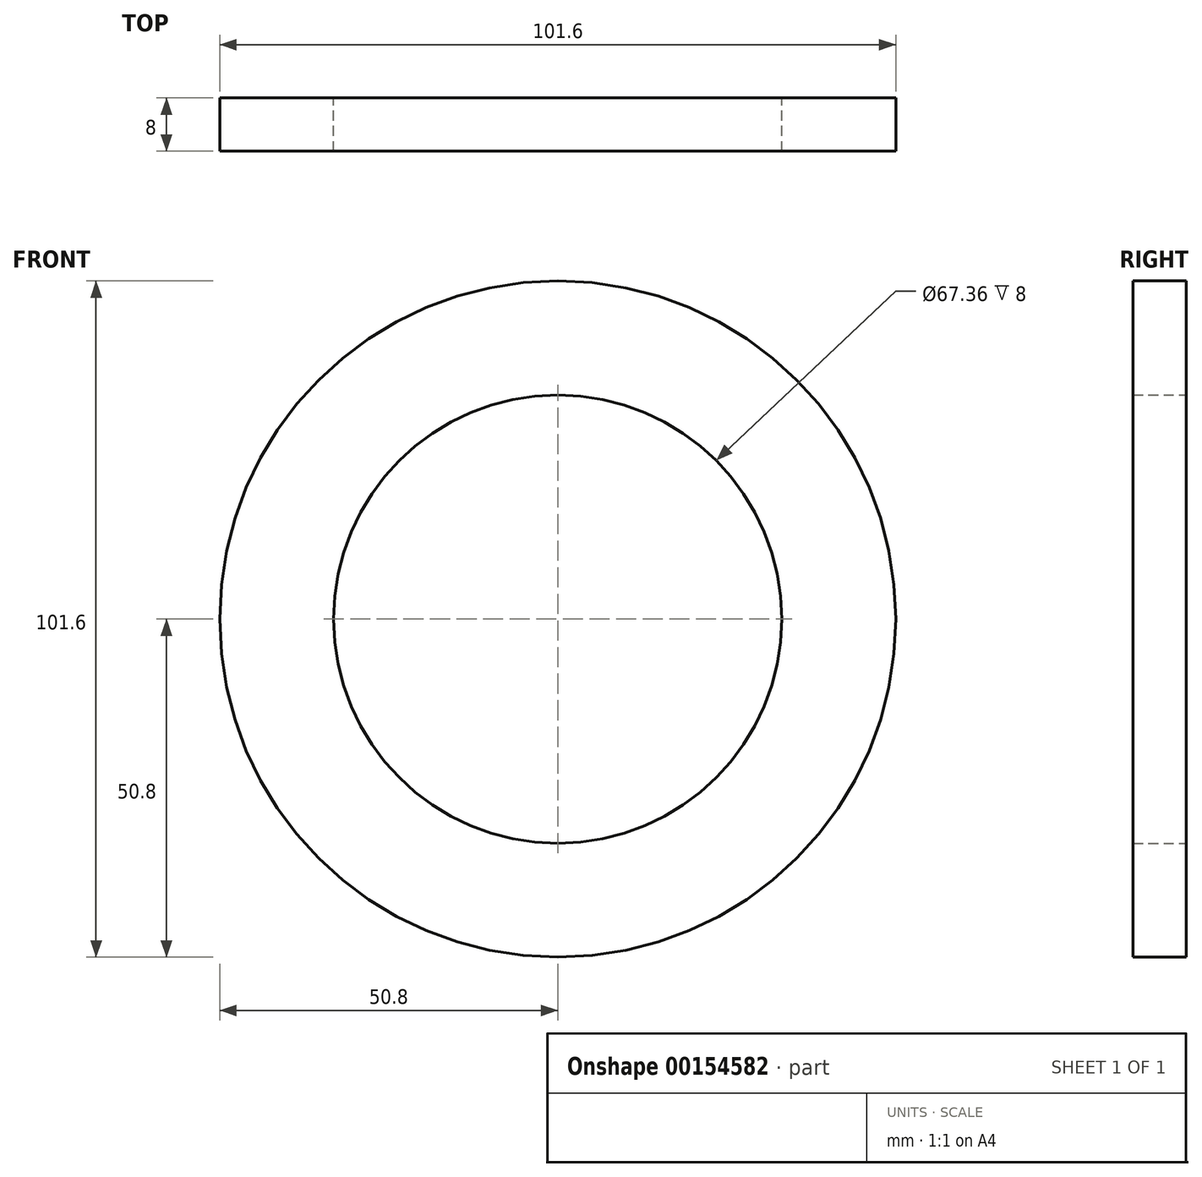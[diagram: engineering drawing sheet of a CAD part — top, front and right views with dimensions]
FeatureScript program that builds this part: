
annotation { "Feature Type Name" : "Feature", "Feature Type Description" : "" }
export const myFeature = defineFeature(function(context is Context, id is Id, definition is map)
    precondition{}
    {
        {
            assignVariable(context, id + "F0", {"name" : "index", "anyValue" : 1});
        }
        {
            assignVariable(context, id + "F1", {"name" : "Diameter", "anyValue" : [3.5, 4, 4.5][getVariable(context, 'index')]});
        }
        {
            var Q0;
            Q0=qCreatedBy(makeId("Front.planeOp"),FACE);
            var sketch = newSketch(context, id + "F2", { "sketchPlane" : qUnion([Q0])});
            skCircle(sketch, "E0", {"center": v(0, 0) * mm, "radius": 50.8 * mm});
            skCircle(sketch, "E1.0", {"center": v(0, 0) * mm, "radius": 33.68 * mm});
            skSolve(sketch);
        }
        {
            var Q0;
            Q0=makeQuery(id+"F2.imprint","IMPRINT",FACE,{"disambiguationData":[TD([[makeQuery(id+"F2.imprint","IMPRINT",EDGE,{"derivedFrom":sQuery(id+"F2.wireOp",EDGE,"E0")}),1.0]])]});
            extrude(context, id + "F3", {"entities" : qUnion([Q0]), "depth" : (2 * getVariable(context, 'Diameter')) * mm});
        }
    });
